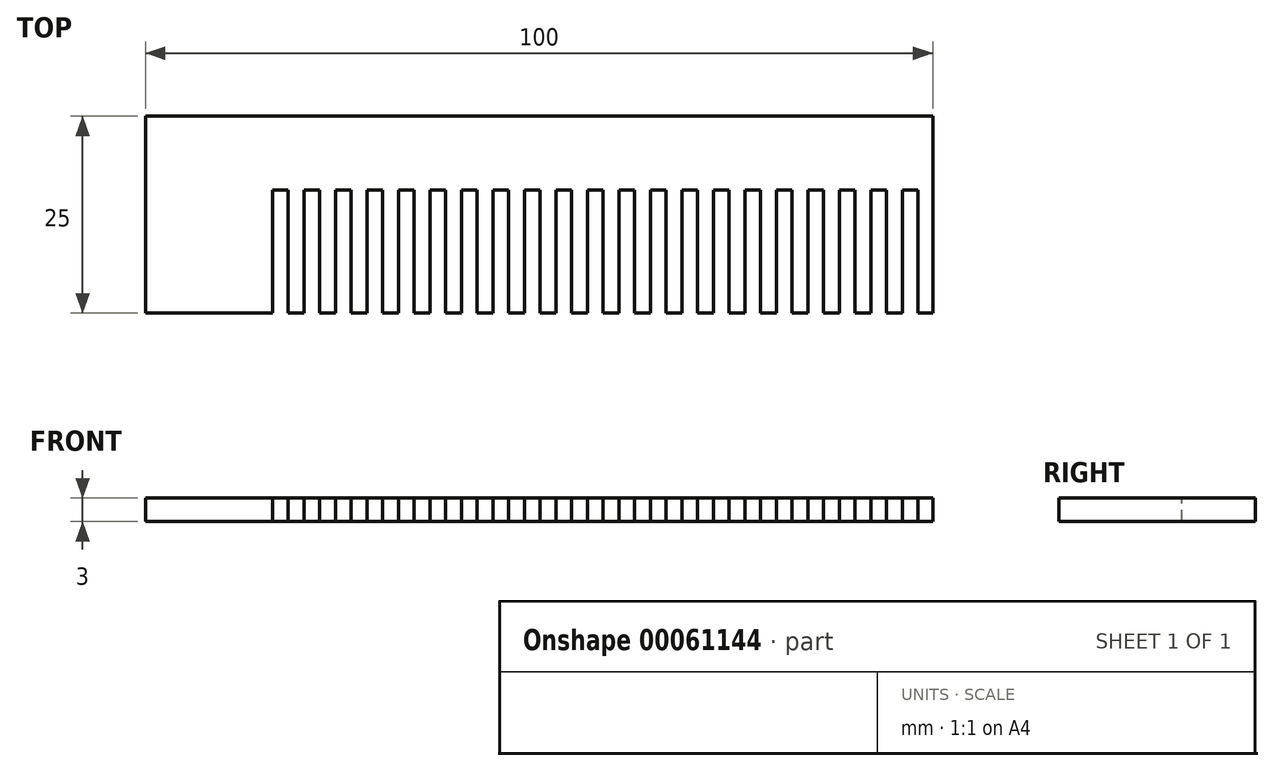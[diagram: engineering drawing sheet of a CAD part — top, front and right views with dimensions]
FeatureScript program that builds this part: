
annotation { "Feature Type Name" : "Feature", "Feature Type Description" : "" }
export const myFeature = defineFeature(function(context is Context, id is Id, definition is map)
    precondition{}
    {
        {
            var Q0;
            Q0=qCreatedBy(makeId("Top.planeOp"),FACE);
            var sketch = newSketch(context, id + "F0", { "sketchPlane" : qUnion([Q0])});
            skLineSegment(sketch, "E0.bottom", {"start": v(-41.92, 48.25) * mm, "end": v(58.08, 48.25) * mm});
            skLineSegment(sketch, "E0.top", {"start": v(-41.92, 23.25) * mm, "end": v(58.08, 23.25) * mm});
            skLineSegment(sketch, "E0.left", {"start": v(-41.92, 48.25) * mm, "end": v(-41.92, 23.25) * mm});
            skLineSegment(sketch, "E0.right", {"start": v(58.08, 48.25) * mm, "end": v(58.08, 23.25) * mm});
            skSolve(sketch);
        }
        {
            var Q0;
            Q0 = qSketchRegion(id + "F0", true);
            extrude(context, id + "F1", {"entities" : qUnion([Q0]), "depth" : 3 * mm});
        }
        {
            var Q0;
            Q0=makeQuery(id+"F1.opExtrude","CAP_FACE",FACE,{"disambiguationData":[OSD([sQuery(id+"F0.wireOp",EDGE,"E0.bottom"),sQuery(id+"F0.wireOp",EDGE,"E0.top"),sQuery(id+"F0.wireOp",EDGE,"E0.left"),sQuery(id+"F0.wireOp",EDGE,"E0.right")])],"isStart":false});
            var sketch = newSketch(context, id + "F2", { "sketchPlane" : qUnion([Q0])});
            skLineSegment(sketch, "E1.bottom", {"start": v(-25.8, 38.87) * mm, "end": v(-23.8, 38.87) * mm});
            skLineSegment(sketch, "E1.top", {"start": v(-25.8, 17.66) * mm, "end": v(-23.8, 17.66) * mm});
            skLineSegment(sketch, "E1.left", {"start": v(-25.8, 38.87) * mm, "end": v(-25.8, 17.66) * mm});
            skLineSegment(sketch, "E1.right", {"start": v(-23.8, 38.87) * mm, "end": v(-23.8, 17.66) * mm});
            skLineSegment(sketch, "E2.1.0.0", {"start": v(-21.8, 38.87) * mm, "end": v(-21.8, 17.66) * mm});
            skLineSegment(sketch, "E2.1.0.1", {"start": v(-21.8, 38.87) * mm, "end": v(-19.8, 38.87) * mm});
            skLineSegment(sketch, "E2.1.0.2", {"start": v(-19.8, 38.87) * mm, "end": v(-19.8, 17.66) * mm});
            skLineSegment(sketch, "E2.1.0.3", {"start": v(-21.8, 17.66) * mm, "end": v(-19.8, 17.66) * mm});
            skLineSegment(sketch, "E2.2.0.0", {"start": v(-17.8, 38.87) * mm, "end": v(-17.8, 17.66) * mm});
            skLineSegment(sketch, "E2.2.0.1", {"start": v(-17.8, 38.87) * mm, "end": v(-15.8, 38.87) * mm});
            skLineSegment(sketch, "E2.2.0.2", {"start": v(-15.8, 38.87) * mm, "end": v(-15.8, 17.66) * mm});
            skLineSegment(sketch, "E2.2.0.3", {"start": v(-17.8, 17.66) * mm, "end": v(-15.8, 17.66) * mm});
            skLineSegment(sketch, "E2.3.0.0", {"start": v(-13.8, 38.87) * mm, "end": v(-13.8, 17.66) * mm});
            skLineSegment(sketch, "E2.3.0.1", {"start": v(-13.8, 38.87) * mm, "end": v(-11.8, 38.87) * mm});
            skLineSegment(sketch, "E2.3.0.2", {"start": v(-11.8, 38.87) * mm, "end": v(-11.8, 17.66) * mm});
            skLineSegment(sketch, "E2.3.0.3", {"start": v(-13.8, 17.66) * mm, "end": v(-11.8, 17.66) * mm});
            skLineSegment(sketch, "E2.4.0.0", {"start": v(-9.8, 38.87) * mm, "end": v(-9.8, 17.66) * mm});
            skLineSegment(sketch, "E2.4.0.1", {"start": v(-9.8, 38.87) * mm, "end": v(-7.8, 38.87) * mm});
            skLineSegment(sketch, "E2.4.0.2", {"start": v(-7.8, 38.87) * mm, "end": v(-7.8, 17.66) * mm});
            skLineSegment(sketch, "E2.4.0.3", {"start": v(-9.8, 17.66) * mm, "end": v(-7.8, 17.66) * mm});
            skLineSegment(sketch, "E2.5.0.0", {"start": v(-5.8, 38.87) * mm, "end": v(-5.8, 17.66) * mm});
            skLineSegment(sketch, "E2.5.0.1", {"start": v(-5.8, 38.87) * mm, "end": v(-3.8, 38.87) * mm});
            skLineSegment(sketch, "E2.5.0.2", {"start": v(-3.8, 38.87) * mm, "end": v(-3.8, 17.66) * mm});
            skLineSegment(sketch, "E2.5.0.3", {"start": v(-5.8, 17.66) * mm, "end": v(-3.8, 17.66) * mm});
            skLineSegment(sketch, "E2.6.0.0", {"start": v(-1.8, 38.87) * mm, "end": v(-1.8, 17.66) * mm});
            skLineSegment(sketch, "E2.6.0.1", {"start": v(-1.8, 38.87) * mm, "end": v(0.2, 38.87) * mm});
            skLineSegment(sketch, "E2.6.0.2", {"start": v(0.2, 38.87) * mm, "end": v(0.2, 17.66) * mm});
            skLineSegment(sketch, "E2.6.0.3", {"start": v(-1.8, 17.66) * mm, "end": v(0.2, 17.66) * mm});
            skLineSegment(sketch, "E2.7.0.0", {"start": v(2.2, 38.87) * mm, "end": v(2.2, 17.66) * mm});
            skLineSegment(sketch, "E2.7.0.1", {"start": v(2.2, 38.87) * mm, "end": v(4.2, 38.87) * mm});
            skLineSegment(sketch, "E2.7.0.2", {"start": v(4.2, 38.87) * mm, "end": v(4.2, 17.66) * mm});
            skLineSegment(sketch, "E2.7.0.3", {"start": v(2.2, 17.66) * mm, "end": v(4.2, 17.66) * mm});
            skLineSegment(sketch, "E2.8.0.0", {"start": v(6.2, 38.87) * mm, "end": v(6.2, 17.66) * mm});
            skLineSegment(sketch, "E2.8.0.1", {"start": v(6.2, 38.87) * mm, "end": v(8.2, 38.87) * mm});
            skLineSegment(sketch, "E2.8.0.2", {"start": v(8.2, 38.87) * mm, "end": v(8.2, 17.66) * mm});
            skLineSegment(sketch, "E2.8.0.3", {"start": v(6.2, 17.66) * mm, "end": v(8.2, 17.66) * mm});
            skLineSegment(sketch, "E2.9.0.0", {"start": v(10.2, 38.87) * mm, "end": v(10.2, 17.66) * mm});
            skLineSegment(sketch, "E2.9.0.1", {"start": v(10.2, 38.87) * mm, "end": v(12.2, 38.87) * mm});
            skLineSegment(sketch, "E2.9.0.2", {"start": v(12.2, 38.87) * mm, "end": v(12.2, 17.66) * mm});
            skLineSegment(sketch, "E2.9.0.3", {"start": v(10.2, 17.66) * mm, "end": v(12.2, 17.66) * mm});
            skLineSegment(sketch, "E2.10.0.0", {"start": v(14.2, 38.87) * mm, "end": v(14.2, 17.66) * mm});
            skLineSegment(sketch, "E2.10.0.1", {"start": v(14.2, 38.87) * mm, "end": v(16.2, 38.87) * mm});
            skLineSegment(sketch, "E2.10.0.2", {"start": v(16.2, 38.87) * mm, "end": v(16.2, 17.66) * mm});
            skLineSegment(sketch, "E2.10.0.3", {"start": v(14.2, 17.66) * mm, "end": v(16.2, 17.66) * mm});
            skLineSegment(sketch, "E2.11.0.0", {"start": v(18.2, 38.87) * mm, "end": v(18.2, 17.66) * mm});
            skLineSegment(sketch, "E2.11.0.1", {"start": v(18.2, 38.87) * mm, "end": v(20.2, 38.87) * mm});
            skLineSegment(sketch, "E2.11.0.2", {"start": v(20.2, 38.87) * mm, "end": v(20.2, 17.66) * mm});
            skLineSegment(sketch, "E2.11.0.3", {"start": v(18.2, 17.66) * mm, "end": v(20.2, 17.66) * mm});
            skLineSegment(sketch, "E2.12.0.0", {"start": v(22.2, 38.87) * mm, "end": v(22.2, 17.66) * mm});
            skLineSegment(sketch, "E2.12.0.1", {"start": v(22.2, 38.87) * mm, "end": v(24.2, 38.87) * mm});
            skLineSegment(sketch, "E2.12.0.2", {"start": v(24.2, 38.87) * mm, "end": v(24.2, 17.66) * mm});
            skLineSegment(sketch, "E2.12.0.3", {"start": v(22.2, 17.66) * mm, "end": v(24.2, 17.66) * mm});
            skLineSegment(sketch, "E2.13.0.0", {"start": v(26.2, 38.87) * mm, "end": v(26.2, 17.66) * mm});
            skLineSegment(sketch, "E2.13.0.1", {"start": v(26.2, 38.87) * mm, "end": v(28.2, 38.87) * mm});
            skLineSegment(sketch, "E2.13.0.2", {"start": v(28.2, 38.87) * mm, "end": v(28.2, 17.66) * mm});
            skLineSegment(sketch, "E2.13.0.3", {"start": v(26.2, 17.66) * mm, "end": v(28.2, 17.66) * mm});
            skLineSegment(sketch, "E2.14.0.0", {"start": v(30.2, 38.87) * mm, "end": v(30.2, 17.66) * mm});
            skLineSegment(sketch, "E2.14.0.1", {"start": v(30.2, 38.87) * mm, "end": v(32.2, 38.87) * mm});
            skLineSegment(sketch, "E2.14.0.2", {"start": v(32.2, 38.87) * mm, "end": v(32.2, 17.66) * mm});
            skLineSegment(sketch, "E2.14.0.3", {"start": v(30.2, 17.66) * mm, "end": v(32.2, 17.66) * mm});
            skLineSegment(sketch, "E2.15.0.0", {"start": v(34.2, 38.87) * mm, "end": v(34.2, 17.66) * mm});
            skLineSegment(sketch, "E2.15.0.1", {"start": v(34.2, 38.87) * mm, "end": v(36.2, 38.87) * mm});
            skLineSegment(sketch, "E2.15.0.2", {"start": v(36.2, 38.87) * mm, "end": v(36.2, 17.66) * mm});
            skLineSegment(sketch, "E2.15.0.3", {"start": v(34.2, 17.66) * mm, "end": v(36.2, 17.66) * mm});
            skLineSegment(sketch, "E2.16.0.0", {"start": v(38.2, 38.87) * mm, "end": v(38.2, 17.66) * mm});
            skLineSegment(sketch, "E2.16.0.1", {"start": v(38.2, 38.87) * mm, "end": v(40.2, 38.87) * mm});
            skLineSegment(sketch, "E2.16.0.2", {"start": v(40.2, 38.87) * mm, "end": v(40.2, 17.66) * mm});
            skLineSegment(sketch, "E2.16.0.3", {"start": v(38.2, 17.66) * mm, "end": v(40.2, 17.66) * mm});
            skLineSegment(sketch, "E2.17.0.0", {"start": v(42.2, 38.87) * mm, "end": v(42.2, 17.66) * mm});
            skLineSegment(sketch, "E2.17.0.1", {"start": v(42.2, 38.87) * mm, "end": v(44.2, 38.87) * mm});
            skLineSegment(sketch, "E2.17.0.2", {"start": v(44.2, 38.87) * mm, "end": v(44.2, 17.66) * mm});
            skLineSegment(sketch, "E2.17.0.3", {"start": v(42.2, 17.66) * mm, "end": v(44.2, 17.66) * mm});
            skLineSegment(sketch, "E2.18.0.0", {"start": v(46.2, 38.87) * mm, "end": v(46.2, 17.66) * mm});
            skLineSegment(sketch, "E2.18.0.1", {"start": v(46.2, 38.87) * mm, "end": v(48.2, 38.87) * mm});
            skLineSegment(sketch, "E2.18.0.2", {"start": v(48.2, 38.87) * mm, "end": v(48.2, 17.66) * mm});
            skLineSegment(sketch, "E2.18.0.3", {"start": v(46.2, 17.66) * mm, "end": v(48.2, 17.66) * mm});
            skLineSegment(sketch, "E2.19.0.0", {"start": v(50.2, 38.87) * mm, "end": v(50.2, 17.66) * mm});
            skLineSegment(sketch, "E2.19.0.1", {"start": v(50.2, 38.87) * mm, "end": v(52.2, 38.87) * mm});
            skLineSegment(sketch, "E2.19.0.2", {"start": v(52.2, 38.87) * mm, "end": v(52.2, 17.66) * mm});
            skLineSegment(sketch, "E2.19.0.3", {"start": v(50.2, 17.66) * mm, "end": v(52.2, 17.66) * mm});
            skLineSegment(sketch, "E2.20.0.0", {"start": v(54.2, 38.87) * mm, "end": v(54.2, 17.66) * mm});
            skLineSegment(sketch, "E2.20.0.1", {"start": v(54.2, 38.87) * mm, "end": v(56.2, 38.87) * mm});
            skLineSegment(sketch, "E2.20.0.2", {"start": v(56.2, 38.87) * mm, "end": v(56.2, 17.66) * mm});
            skLineSegment(sketch, "E2.20.0.3", {"start": v(54.2, 17.66) * mm, "end": v(56.2, 17.66) * mm});
            skLineSegment(sketch, "E2.direction1", {"start": v(-25.8, 17.66) * mm, "end": v(-21.8, 17.66) * mm, "construction": true});
            skSolve(sketch);
        }
        {
            var Q0;
            Q0 = qSketchRegion(id + "F2", true);
            extrude(context, id + "F3", {"entities" : qUnion([Q0]), "operationType" : NewBodyOperationType.REMOVE, "oppositeDirection" : true, "depth" : 25 * mm});
        }
    });
